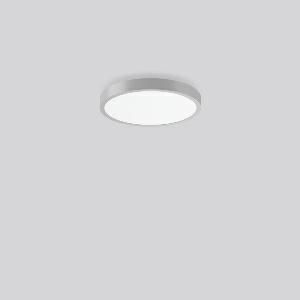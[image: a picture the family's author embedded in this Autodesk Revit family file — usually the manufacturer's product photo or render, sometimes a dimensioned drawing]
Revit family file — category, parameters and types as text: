
# Revit family: triona_round_a_312420_004_1_730_ef7c
name_source: partatom
category: Lighting Fixtures
units: mm (PartAtom-declared; Revit-internal decimal feet)

## family parameters
Cut with Voids When Loaded = No
Host = Face
Light Source = No
Part Type = Normal
Room Calculation Point = No
Round Connector Dimension = Use Diameter
Shared = No

## types (1)
- TRIONA round A (1 x LED Modul 840, 6050 lm, 4000)
    Apparent Load = 64 VA
    CIE Flux Codes = 49 80 96 82 100
    Color Rendering = 80
    Color Temperature = 4000
    Default Elevation = 1800 mm
    Description = Series: TRIONA round
Decorative round LED surface-mounted luminaire. Flat, seamless frame: aluminium extrusion profile, powder coated. Cover made of sheet steel, powder-coated. Direct light emission through a diffuser plastic opal. Indirect light emission through a flush diffuser made of satin-finish plastic. Lightguide and diffuser made of non-yellowing plastic (PMMA). Lateral light emission (RZB SIDELITE technology) for above-average homogeneous light distribution. Direct 70%, indirect 30% light emission. Suitable for Ceiling mounting, Wall (surface). Tool-free mounting via bayonet connection. Electronic ballast included. Very easy installation thanks to Plug+Play connection. With Casambi smart+free Bluetooth control for wireless network and operation using Android / iOS devices, free app available for download. 
Colour: silver, matt (approx. RAL 9006)
Diameter: 461 mm
Height: 88 mm
Lamp: LED
Socket: without socket
Colour temperature: 4000K
Colour rendering index (CRI): 80
System power: 64 W
Rated luminous flux: 6050 lm
Luminous efficiency: 95 lm/W
Control gear: Dimmable Bluetooth converter
Protection class: I
Type of protection: IP 20
    Height = 88 mm
    Lamp = 1 x LED Modul 840
    Lamp Light Flux = 6050 lm
    Lamp count = 1
    Length = 461 mm
    Lifetime = 50000 h
    Luminous efficacy = 95 lm/W
    Manufacturer = RZB
    ModVariant = No
    Model = 312420.004.1.730
    Mounting Place = Ceiling
    Mounting Type = Surface mounted
    Number of Poles = 1
    OnlyDefault = Yes
    Power Factor = 1
    Product Name = TRIONA round A
    Product group = Surface mounted modular luminaires
    ProductGroupID = 306
    Protection Class = Protection class I
    Protection Degree = IP 20
    RLX_Detail_Level = 1
    RLX_Emergency_Light_Flux = 0 lm
    RLX_Emergency_Type = 0
    RLX_Emergency_Type_DB = No
    RlxData = <blob elided: 37557 chars, md5=4d6a2b96>
    Socket = socket
    Standby Power = 0 W
    System Light Flux = 6050 lm
    System Power = 64 W
    Type Comments = Product without accessories
    Type Image = 312420.004.jpg
    URL = http://relux.com
    VarID = ---
    Voltage = 230 V
    Voltage Range = 220-240 V
    Weight = 0.00 kg
    Width = 0 mm  [stored 0 ft]

note: [stored X ft] marks values corroborated as IEEE doubles in the binary element streams (Revit-internal decimal feet)

## geometry (parser evidence)
native form markers: Blend x4, Sweep x12
no freeform markers — native parametric forms only
